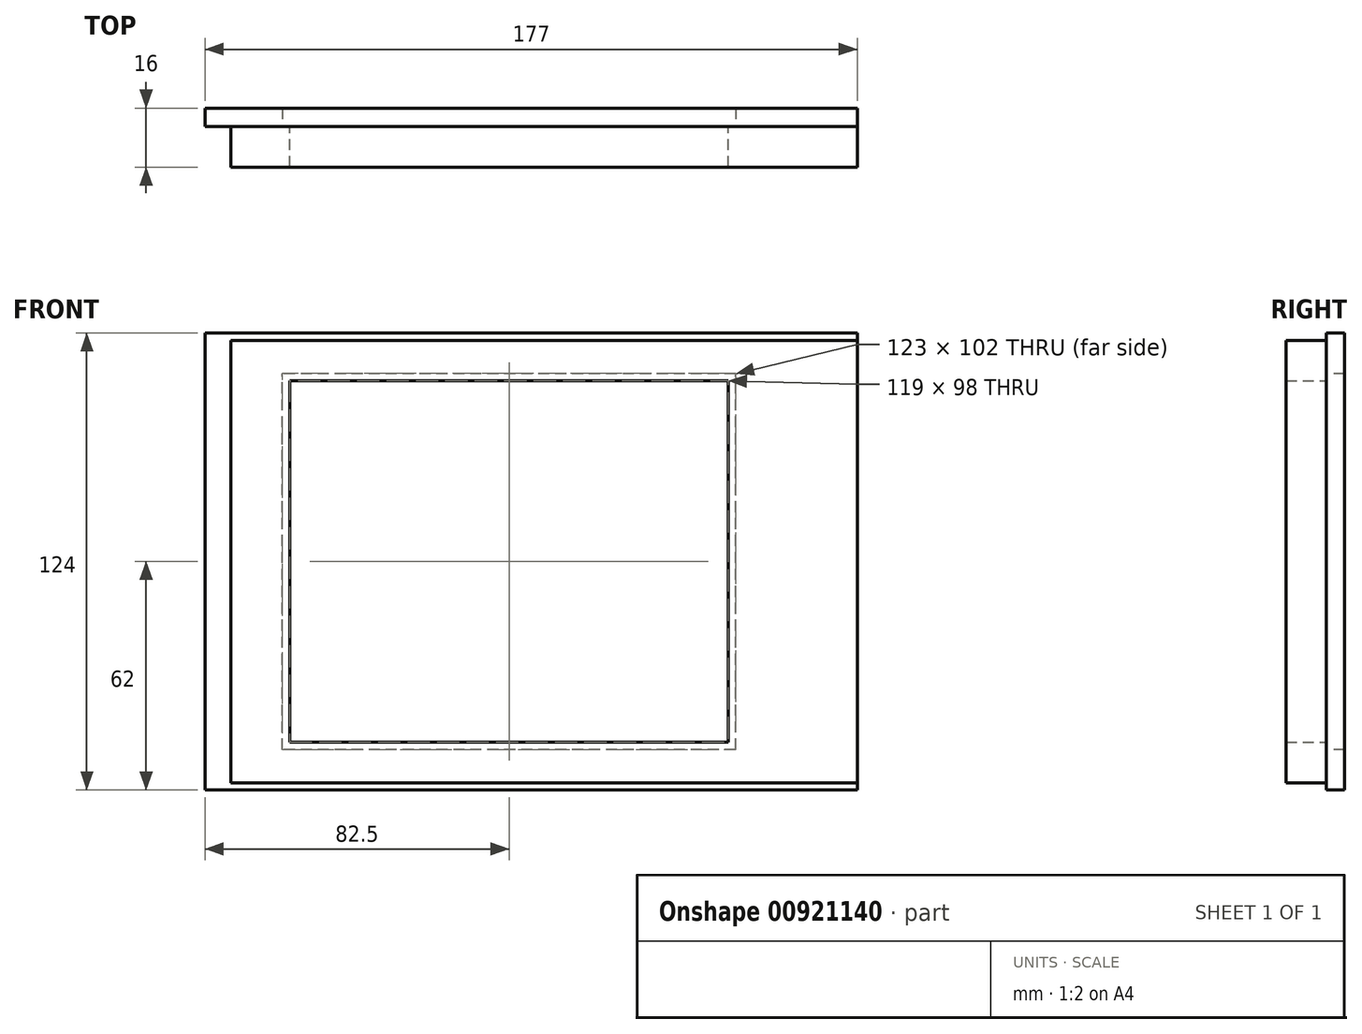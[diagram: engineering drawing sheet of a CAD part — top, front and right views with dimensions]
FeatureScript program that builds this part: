
annotation { "Feature Type Name" : "Feature", "Feature Type Description" : "" }
export const myFeature = defineFeature(function(context is Context, id is Id, definition is map)
    precondition{}
    {
        {
            var Q0;
            Q0=qCreatedBy(makeId("Front.planeOp"),FACE);
            var sketch = newSketch(context, id + "F0", { "sketchPlane" : qUnion([Q0])});
            skLineSegment(sketch, "E0.bottom", {"start": v(59.5, -49) * mm, "end": v(-59.5, -49) * mm});
            skLineSegment(sketch, "E0.top", {"start": v(59.5, 49) * mm, "end": v(-59.5, 49) * mm});
            skLineSegment(sketch, "E0.left", {"start": v(59.5, -49) * mm, "end": v(59.5, 49) * mm});
            skLineSegment(sketch, "E0.right", {"start": v(-59.5, -49) * mm, "end": v(-59.5, 49) * mm});
            skPoint(sketch, "E0.middle", {"position": v(0, 0) * mm});
            skLineSegment(sketch, "E1.bottom", {"start": v(-75.5, 60) * mm, "end": v(94.5, 60) * mm});
            skLineSegment(sketch, "E1.top", {"start": v(-75.5, -60) * mm, "end": v(94.5, -60) * mm});
            skLineSegment(sketch, "E1.left", {"start": v(-75.5, 60) * mm, "end": v(-75.5, -60) * mm});
            skLineSegment(sketch, "E1.right", {"start": v(94.5, 60) * mm, "end": v(94.5, -60) * mm});
            skLineSegment(sketch, "E2", {"start": v(-126.6, 0) * mm, "end": v(149.06, 0) * mm, "construction": true});
            skLineSegment(sketch, "E3", {"start": v(0, 104.03) * mm, "end": v(0, -124.25) * mm, "construction": true});
            skSolve(sketch);
        }
        {
            var Q0;
            Q0=makeQuery(id+"F0.imprint","IMPRINT",FACE,{"disambiguationData":[TD([[makeQuery(id+"F0.imprint","IMPRINT",EDGE,{"derivedFrom":sQuery(id+"F0.wireOp",EDGE,"E0.bottom")}),1.0]])]});
            extrude(context, id + "F1", {"entities" : qUnion([Q0]), "depth" : 11 * mm, "offsetDistance" : 25 * mm});
        }
        {
            var Q0;
            Q0=qCreatedBy(makeId("Front.planeOp"),FACE);
            var sketch = newSketch(context, id + "F2", { "sketchPlane" : qUnion([Q0])});
            skLineSegment(sketch, "E4.bottom", {"start": v(-82.5, 62) * mm, "end": v(94.5, 62) * mm});
            skLineSegment(sketch, "E4.top", {"start": v(-82.5, -62) * mm, "end": v(94.5, -62) * mm});
            skLineSegment(sketch, "E4.left", {"start": v(-82.5, 62) * mm, "end": v(-82.5, -62) * mm});
            skLineSegment(sketch, "E4.right", {"start": v(94.5, 62) * mm, "end": v(94.5, -62) * mm});
            skLineSegment(sketch, "E5", {"start": v(-127.47, 0) * mm, "end": v(155.52, 0) * mm, "construction": true});
            skLineSegment(sketch, "E6", {"start": v(-75.5, 62) * mm, "end": v(-75.5, -62) * mm});
            skLineSegment(sketch, "E7", {"start": v(0, 109.18) * mm, "end": v(0, -123.28) * mm, "construction": true});
            skLineSegment(sketch, "E8.0", {"start": v(59.5, 49) * mm, "end": v(-59.5, 49) * mm, "construction": true});
            skLineSegment(sketch, "E9.0", {"start": v(-59.5, -49) * mm, "end": v(-59.5, 49) * mm, "construction": true});
            skLineSegment(sketch, "E10.0", {"start": v(59.5, -49) * mm, "end": v(-59.5, -49) * mm, "construction": true});
            skLineSegment(sketch, "E11.0", {"start": v(59.5, -49) * mm, "end": v(59.5, 49) * mm, "construction": true});
            skLineSegment(sketch, "E12.bottom", {"start": v(61.5, -51) * mm, "end": v(-61.5, -51) * mm});
            skLineSegment(sketch, "E12.top", {"start": v(61.5, 51) * mm, "end": v(-61.5, 51) * mm});
            skLineSegment(sketch, "E12.left", {"start": v(61.5, -51) * mm, "end": v(61.5, 51) * mm});
            skLineSegment(sketch, "E12.right", {"start": v(-61.5, -51) * mm, "end": v(-61.5, 51) * mm});
            skPoint(sketch, "E12.middle", {"position": v(0, 0) * mm});
            skLineSegment(sketch, "E13.0", {"start": v(-75.5, 60) * mm, "end": v(94.5, 60) * mm, "construction": true});
            skLineSegment(sketch, "E14.0", {"start": v(-75.5, -60) * mm, "end": v(94.5, -60) * mm, "construction": true});
            skSolve(sketch);
        }
        {
            var Q0;
            {var subQ0=sQuery(id+"F2.wireOp",EDGE,"E4.right");Q0=makeQuery(id+"F2.imprint","IMPRINT",FACE,{"disambiguationData":[TD([[makeQuery(id+"F2.imprint","IMPRINT",EDGE,{"derivedFrom":subQ0}),-1.0]])]});}
            var Q1;
            {var subQ0=sQuery(id+"F2.wireOp",EDGE,"E4.left");Q1=makeQuery(id+"F2.imprint","IMPRINT",FACE,{"disambiguationData":[TD([[makeQuery(id+"F2.imprint","IMPRINT",EDGE,{"derivedFrom":subQ0}),1.0]])]});}
            extrude(context, id + "F3", {"entities" : qUnion([Q0, Q1]), "oppositeDirection" : true, "depth" : 5 * mm, "offsetDistance" : 25 * mm});
        }
    });
